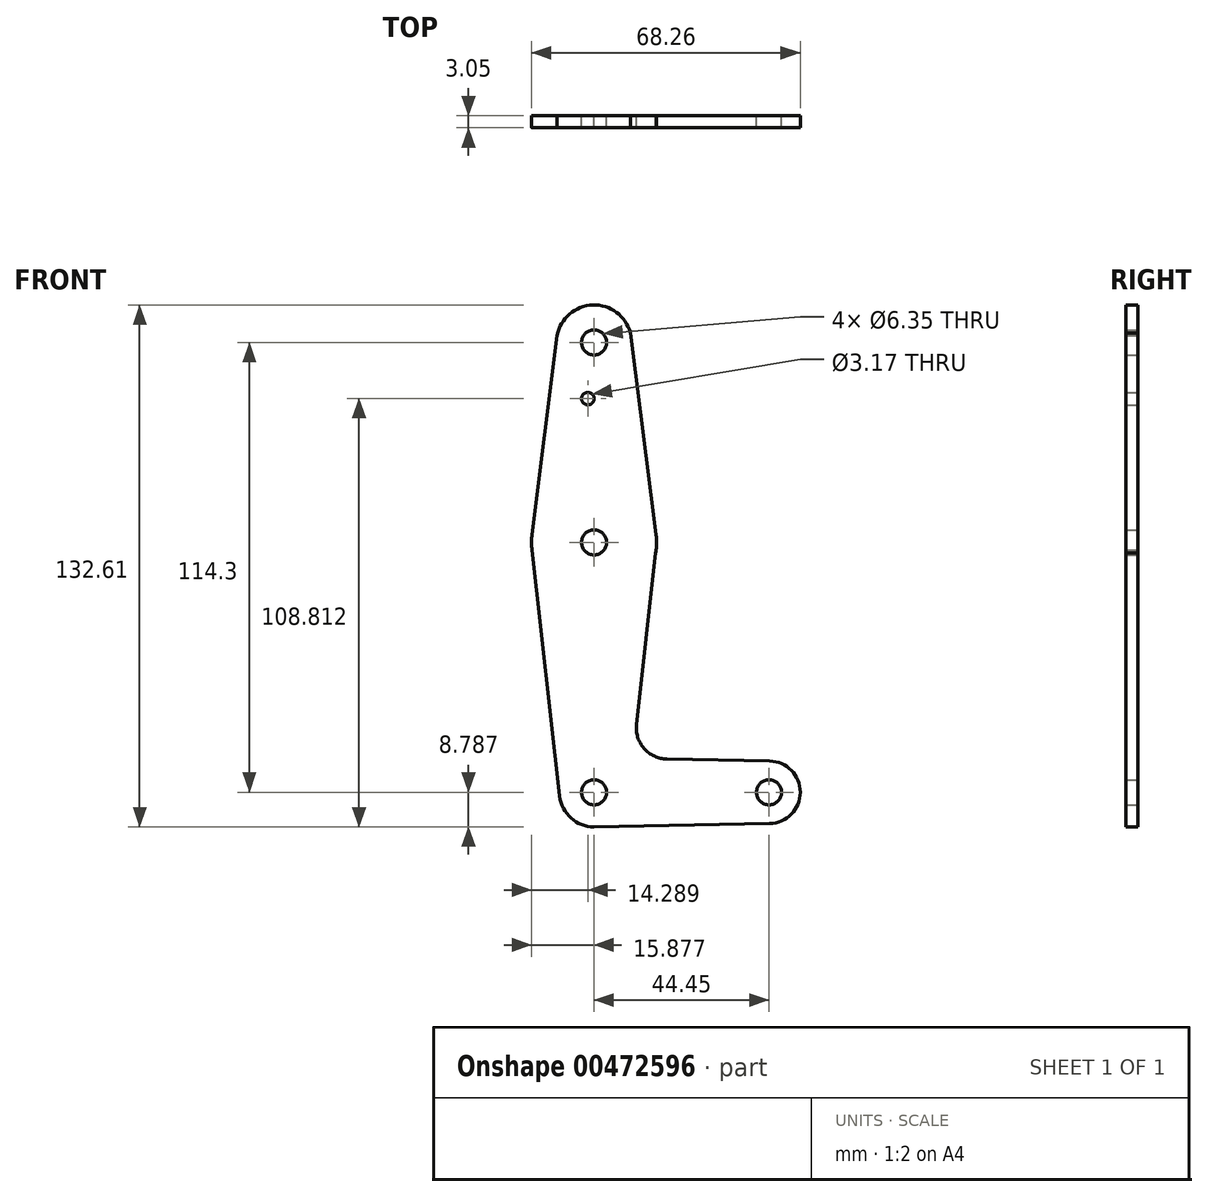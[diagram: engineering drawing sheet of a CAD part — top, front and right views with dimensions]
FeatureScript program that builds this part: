
annotation { "Feature Type Name" : "Feature", "Feature Type Description" : "" }
export const myFeature = defineFeature(function(context is Context, id is Id, definition is map)
    precondition{}
    {
        {
            var Q0;
            Q0=qCreatedBy(makeId("Front.planeOp"),FACE);
            var sketch = newSketch(context, id + "F0", { "sketchPlane" : qUnion([Q0])});
            skLineSegment(sketch, "E0", {"start": v(-26.08, 60.7) * mm, "end": v(-26.08, -53.6) * mm, "construction": true});
            skLineSegment(sketch, "E1", {"start": v(-26.08, -53.6) * mm, "end": v(18.37, -53.6) * mm, "construction": true});
            skCircle(sketch, "E2", {"center": v(18.37, -53.6) * mm, "radius": 7.94 * mm});
            skCircle(sketch, "E3", {"center": v(-26.08, -53.6) * mm, "radius": 8.79 * mm});
            skCircle(sketch, "E4", {"center": v(-26.08, 9.9) * mm, "radius": 15.88 * mm});
            skCircle(sketch, "E5", {"center": v(-26.08, 60.7) * mm, "radius": 9.53 * mm});
            skLineSegment(sketch, "E6", {"start": v(-35.44, 62.48) * mm, "end": v(-41.83, 11.9) * mm});
            skLineSegment(sketch, "E7", {"start": v(-41.84, 7.98) * mm, "end": v(-34.81, -54.57) * mm});
            skLineSegment(sketch, "E8", {"start": v(-16.87, 63.13) * mm, "end": v(-10.34, 11.92) * mm});
            skLineSegment(sketch, "E9", {"start": v(-10.43, 7.24) * mm, "end": v(-15.3, -36.33) * mm});
            skLineSegment(sketch, "E10", {"start": v(-7.56, -45.16) * mm, "end": v(18.52, -45.66) * mm});
            skLineSegment(sketch, "E11", {"start": v(-26.1, -62.38) * mm, "end": v(18.52, -61.53) * mm});
            skCircle(sketch, "E12", {"center": v(-26.08, 60.7) * mm, "radius": 3.18 * mm});
            skCircle(sketch, "E13", {"center": v(-27.67, 46.43) * mm, "radius": 1.59 * mm});
            skArc(sketch, "E14.filletArc", {"start": v(-15.3, -36.33) * mm, "mid": v(-13.38, -42.45) * mm, "end": v(-7.56, -45.16) * mm});
            skCircle(sketch, "E15", {"center": v(-26.08, 9.9) * mm, "radius": 3.18 * mm});
            skCircle(sketch, "E16", {"center": v(-26.08, -53.6) * mm, "radius": 3.18 * mm});
            skCircle(sketch, "E17", {"center": v(18.37, -53.6) * mm, "radius": 3.18 * mm});
            skSolve(sketch);
        }
        {
            var Q0;
            {var subQ0=sQuery(id+"F0.wireOp",EDGE,"E2");var subQ1=makeQuery(id+"F0.imprint","INTERSECT",VERTEX,{"derivedFrom":[subQ0,sQuery(id+"F0.wireOp",EDGE,"E10")]});Q0=makeQuery(id+"F0.imprint","IMPRINT",FACE,{"disambiguationData":[TD([[makeQuery(id+"F0.imprint","IMPRINT",EDGE,{"disambiguationData":[TD([[subQ1,-1.0]])],"derivedFrom":subQ0}),1.0]])]});}
            var Q1;
            {var subQ0=sQuery(id+"F0.wireOp",EDGE,"E11");var subQ1=sQuery(id+"F0.wireOp",EDGE,"E3");var subQ2=makeQuery(id+"F0.imprint","INTERSECT",VERTEX,{"disambiguationData":[OD(0.0)],"derivedFrom":[subQ1,subQ0]});Q1=makeQuery(id+"F0.imprint","IMPRINT",FACE,{"disambiguationData":[TD([[makeQuery(id+"F0.imprint","IMPRINT",EDGE,{"disambiguationData":[TD([[subQ2,-1.0]])],"derivedFrom":subQ1}),1.0]])]});}
            var Q2;
            {var subQ0=sQuery(id+"F0.wireOp",EDGE,"E6");var subQ1=sQuery(id+"F0.wireOp",EDGE,"E5");var subQ2=makeQuery(id+"F0.imprint","INTERSECT",VERTEX,{"disambiguationData":[OD(0.0)],"derivedFrom":[subQ1,subQ0]});Q2=makeQuery(id+"F0.imprint","IMPRINT",FACE,{"disambiguationData":[TD([[makeQuery(id+"F0.imprint","IMPRINT",EDGE,{"disambiguationData":[TD([[subQ2,-1.0]])],"derivedFrom":subQ1}),1.0]])]});}
            var Q3;
            {var subQ0=sQuery(id+"F0.wireOp",EDGE,"E8");var subQ1=sQuery(id+"F0.wireOp",EDGE,"E5");var subQ2=makeQuery(id+"F0.imprint","INTERSECT",VERTEX,{"disambiguationData":[OD(0.0)],"derivedFrom":[subQ1,subQ0]});Q3=makeQuery(id+"F0.imprint","IMPRINT",FACE,{"disambiguationData":[TD([[makeQuery(id+"F0.imprint","IMPRINT",EDGE,{"disambiguationData":[TD([[subQ2,1.0]])],"derivedFrom":subQ1}),1.0]])]});}
            var Q4;
            {var subQ0=sQuery(id+"F0.wireOp",EDGE,"E3");var subQ1=makeQuery(id+"F0.imprint","INTERSECT",VERTEX,{"derivedFrom":[subQ0,sQuery(id+"F0.wireOp",EDGE,"E7")]});Q4=makeQuery(id+"F0.imprint","IMPRINT",FACE,{"disambiguationData":[TD([[makeQuery(id+"F0.imprint","IMPRINT",EDGE,{"disambiguationData":[TD([[subQ1,-1.0]])],"derivedFrom":subQ0}),1.0]])]});}
            var Q5;
            {var subQ0=sQuery(id+"F0.wireOp",EDGE,"E4");var subQ1=makeQuery(id+"F0.imprint","INTERSECT",VERTEX,{"derivedFrom":[subQ0,sQuery(id+"F0.wireOp",EDGE,"E6")]});Q5=makeQuery(id+"F0.imprint","IMPRINT",FACE,{"disambiguationData":[TD([[makeQuery(id+"F0.imprint","IMPRINT",EDGE,{"disambiguationData":[TD([[subQ1,1.0]])],"derivedFrom":subQ0}),1.0]])]});}
            var Q6;
            {var subQ0=sQuery(id+"F0.wireOp",EDGE,"E7");Q6=makeQuery(id+"F0.imprint","IMPRINT",FACE,{"disambiguationData":[TD([[makeQuery(id+"F0.imprint","IMPRINT",EDGE,{"derivedFrom":subQ0}),1.0]])]});}
            var Q7;
            {var subQ5=sQuery(id+"F0.wireOp",EDGE,"E6");var subQ6=sQuery(id+"F0.wireOp",EDGE,"E4");var subQ7=makeQuery(id+"F0.imprint","INTERSECT",VERTEX,{"derivedFrom":[subQ6,subQ5]});Q7=makeQuery(id+"F0.imprint","IMPRINT",FACE,{"disambiguationData":[TD([[makeQuery(id+"F0.imprint","IMPRINT",EDGE,{"disambiguationData":[TD([[subQ7,1.0]])],"derivedFrom":subQ6}),-1.0]])]});}
            var Q8;
            Q8=makeQuery(id+"F0.imprint","IMPRINT",FACE,{"disambiguationData":[TD([[makeQuery(id+"F0.imprint","IMPRINT",EDGE,{"derivedFrom":sQuery(id+"F0.wireOp",EDGE,"E12")}),-1.0]])]});
            extrude(context, id + "F1", {"entities" : qUnion([Q0, Q1, Q2, Q3, Q4, Q5, Q6, Q7, Q8]), "depth" : 3.05 * mm});
        }
    });
